# Revit family: Grohe_ShowerSystem_EuphoriaSmartcontrolSystem310Duo_22120KF0
name_source: partatom
category: Plumbing Fixtures
units: mm (PartAtom-declared; Revit-internal decimal feet)

## family parameters
Cut with Voids When Loaded = No
Host = Face
OmniClass Number = 23.45.05.00
OmniClass Title = Sanitary Equipment
Part Type = Normal
Room Calculation Point = No
Round Connector Dimension = Use Diameter
Shared = No

## types (1)
- EUPHORIA SMARTCONTROL SYSTEM 310 DUO Shower System (22120KF0)
    Assembly Code = D2010
    AssetType = Fixed
    BIMObjectName = Grohe_ShowerSystem_EuphoriaSmartcontrolSystem310Duo_22120KF0
    CO2NeutralProduction = GROHE is one of the first leading manufacturer within the sanitary industry having a CO2-neutral production.
    CW Connection = Yes
    ClassificationName = Uniclass2015
    ClassificationValue = Pr_40_20_87_75
    Color = Matt Black
    Cost = 0 $
    Default Elevation = 0 mm  [stored 0 ft]
    Description = EUPHORIA SMARTCONTROL SYSTEM 310 DUO Shower System
    DimensionsDocumentLink = https://cdn.cloud.grohe.com
    DocumentationCertificates = https://www.bimstore.co
    DocumentationInstallationGuide = https://www.bimstore.co
    DocumentationLiterature = https://www.bimstore.co
    DocumentationMaintenance = https://www.bimstore.co
    DocumentationTechnical = https://www.bimstore.co
    DurationUnit = Years
    EF000008 = 306 mm
    EF000040 = 1104 mm
    EF000049 = 441 mm
    EF000051 = 310
    EF000634 = 0.0 Pa
    EF001707 = 70 °C
    EF002169 = Other
    EF002286 = External thread
    EF002671 = Other
    EF003454 = FALSE
    EF003829 = FALSE
    EF005084 = Wall
    EF006009 = TRUE
    EF006013 = FALSE
    EF006974 = Thermostatic
    EF020103 = FALSE
    EF020785 = 1/2 inch
    EF021457 = FALSE
    EF021607 = FALSE
    EF021720 = TRUE
    EF021760 = TRUE
    EF022168 = TRUE
    EF022284 = FALSE
    EF023051 = Mechanical
    EF023061 = 0.0 Pa
    EF023686 = not applicable
    EF023957 = TRUE
    EF024792 = FALSE
    EF024885 = TRUE
    EF024921 = FALSE
    EF025090 = FALSE
    EF025091 = FALSE
    EF025092 = 0
    EF025093 = not applicable
    EF025094 = 1750
    EF025095 = not applicable
    EF025096 = TRUE
    EF025097 = 0.0 L/s
    EFSE0002 = FALSE
    Ecojoy = No
    ExpectedLife = 0
    FullRecyclabilityOfPlastic = All plastic components are fully recyclable
    GROHESocialCommittment = green.grohe.com/social_engagement
    GROHESustainability = green.grohe.com
    HW Connection = Yes
    IfcExportAs = IfcPipeFitting
    IfcExportType = IfcPipeFittingType
    Keynote = N13
    Manufacturer = Grohe
    ManufacturerName = Grohe
    Model = EUPHORIA SMARTCONTROL SYSTEM 310 DUO Shower System
    ModelNumber = 22120KF0
    ModelReference = EUPHORIA SMARTCONTROL SYSTEM 310 DUO Shower System
    NBSDescription = Shower fittings package
    NBSObjectName = Grohe - Shower fittings package
    NBSReference = 45-35-70/330
    NominalDepth = 0 mm  [stored 0 ft]
    NominalHeight = 0 mm  [stored 0 ft]
    NominalLength = 0 mm  [stored 0 ft]
    PQDiagramLink = https://cdn.cloud.grohe.com
    PrimaryMaterial = Grohe_MattBlack
    ProductDescription = consisting of:

horizontal 450 mm shower arm

upper bracket adjustable for minimal adaption to existing drilling holes

exposed SmartControl thermostat

allows change between:

head shower Rainshower SmartActive 310

2 spray patterns: GROHE PureRain, ActiveRain

hand shower Euphoria 110 Massage, spray plate phantom black

3 spray patterns:

Rain, SmartRain, Massage

adjustable in height with gliding element

Silverflex shower hose 1750 mm (28 388)

GROHE DreamSpray perfect spray pattern

GROHE Long-Life Shine finish

GROHE CoolTouch no risk of scalding

GROHE TurboStat compact cartridge with wax thermoelement

GROHE ProGrip with knurl structure

GROHE Water Saving - Less water, perfect flow

GROHE SafeStop at 38°C

GROHE SafeStop Plus optional temperature limiter at 43°C included

GROHE SmartControl push for ON-OFF, turn for volume adjustment from GROHE Water Saving to Full Flow

integrated GROHE EasyReach shower tray

SpeedClean anti-limescale system

Inner WaterGuide for a longer life

TwistStop to prevent hose from twisting

suitable for instantaneous heaters from 18 kW/h

minimum flow rate 7 l/min
    ProductNumber = 22120KF0
    ProductPageURL = https://www.grohe.co.uk
    ProductShortText = Shower system with thermostat for wall mounting
    ProductType = Shower System
    ProductionYear = 2023
    SustainabilityAward = green.grohe.com/awards
    SustainabilityReport = green.grohe.com/reporting
    TPIDocumentLink = https://cdn.cloud.grohe.com
    Type Comments = EUPHORIA SMARTCONTROL SYSTEM 310 DUO Shower System
    TypeName = EUPHORIA SMARTCONTROL SYSTEM 310 DUO Shower System
    URL = https://www.grohe.co.uk
    Vent Connection = No
    WarrantyDurationLabor = 0
    WarrantyDurationParts = 0
    WarrantyDurationUnit = Years
    Waste Connection = No
    _BSBibleVersion = 17
    _BimSpecGuid = 0
    _CurrentRevision = 1
    _DistributedBy = https://www.bimstore.co
    _ObjectUserGuide = https://www.bimstore.co

note: [stored X ft] marks values corroborated as IEEE doubles in the binary element streams (Revit-internal decimal feet)

## geometry (parser evidence)
native form markers: Sweep x3
no freeform markers — native parametric forms only
